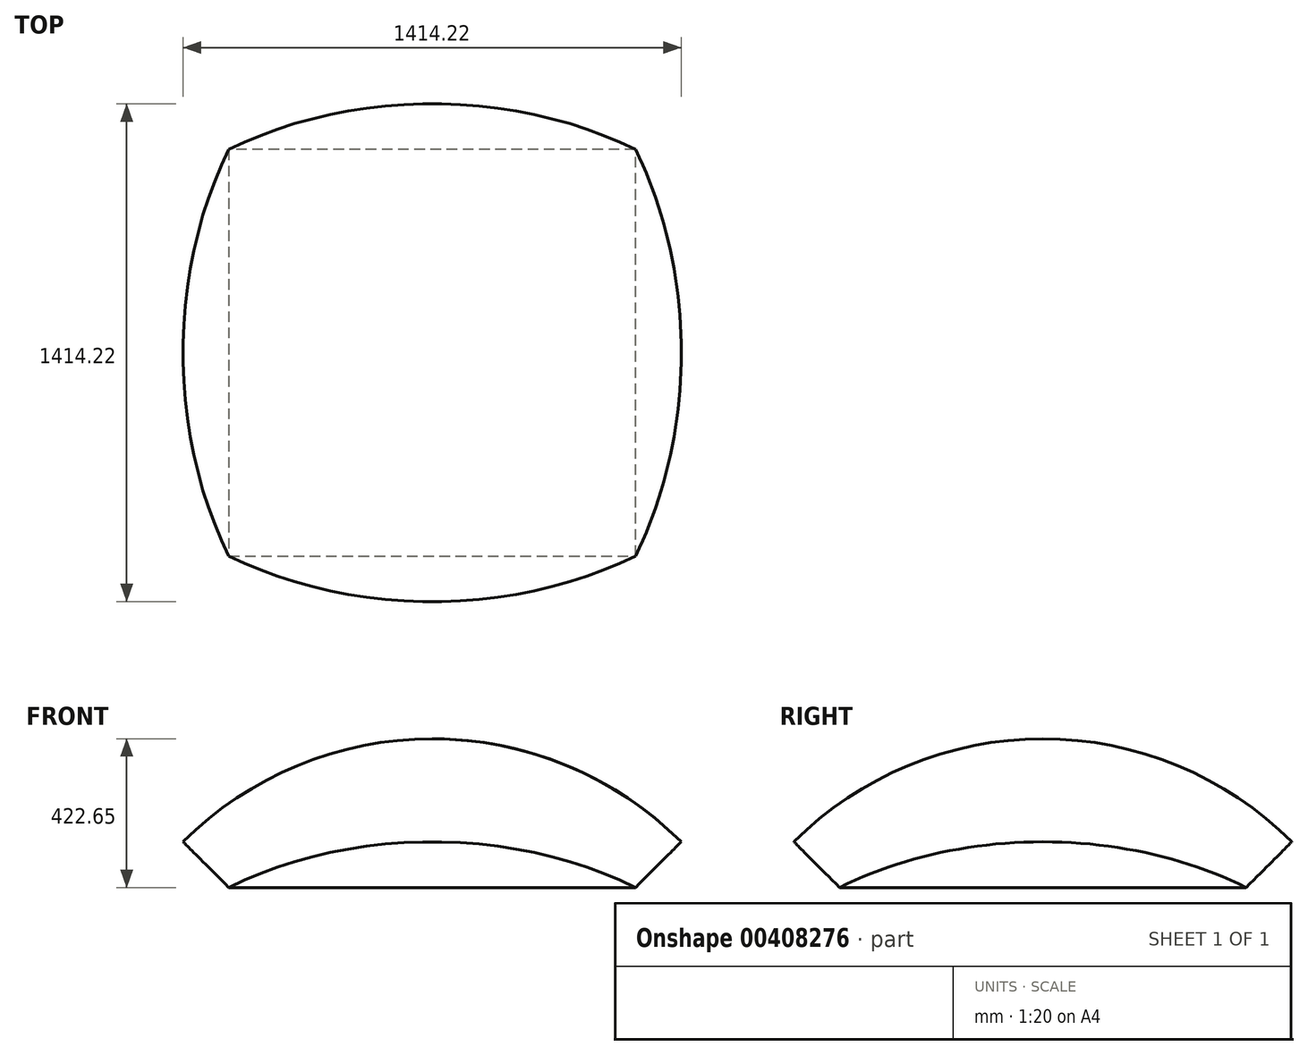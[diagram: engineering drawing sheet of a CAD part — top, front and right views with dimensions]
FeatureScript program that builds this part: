
annotation { "Feature Type Name" : "Feature", "Feature Type Description" : "" }
export const myFeature = defineFeature(function(context is Context, id is Id, definition is map)
    precondition{}
    {
        {
            var Q0;
            Q0=qCreatedBy(makeId("Front.planeOp"),FACE);
            var sketch = newSketch(context, id + "F0", { "sketchPlane" : qUnion([Q0])});
            skArc(sketch, "E0", {"start": v(0, 1000) * mm, "mid": v(-1000, 0) * mm, "end": v(0, -1000) * mm});
            skLineSegment(sketch, "E1", {"start": v(0, 1000) * mm, "end": v(0, -1000) * mm});
            skSolve(sketch);
        }
        {
            var Q0;
            Q0 = qSketchRegion(id + "F0", true);
            var Q1;
            Q1=sQuery(id+"F0.wireOp",EDGE,"E1");
            revolve(context, id + "F1", {"entities" : qUnion([Q0]), "axis" : qUnion([Q1]), "revolveType" : RevolveType.FULL});
        }
        {
            var Q0;
            Q0=qCreatedBy(makeId("Front.planeOp"),FACE);
            var sketch = newSketch(context, id + "F2", { "sketchPlane" : qUnion([Q0])});
            skLineSegment(sketch, "E2", {"start": v(-1100, 1100) * mm, "end": v(-1100, -1100) * mm});
            skLineSegment(sketch, "E3", {"start": v(1100, -1100) * mm, "end": v(1100, 1100) * mm});
            skLineSegment(sketch, "E4", {"start": v(1100, 1100) * mm, "end": v(0, 0) * mm});
            skLineSegment(sketch, "E5", {"start": v(0, 0) * mm, "end": v(-1100, 1100) * mm});
            skLineSegment(sketch, "E6", {"start": v(-1100, -1100) * mm, "end": v(1100, -1100) * mm});
            skSolve(sketch);
        }
        {
            var Q0;
            Q0 = qSketchRegion(id + "F2", true);
            extrude(context, id + "F3", {"entities" : qUnion([Q0]), "operationType" : NewBodyOperationType.REMOVE, "endBound" : BoundingType.SYMMETRIC, "oppositeDirection" : true, "depth" : 2200 * mm, "hasSecondDirection" : true, "secondDirectionBound" : SecondDirectionBoundingType.THROUGH_ALL, "secondDirectionOppositeDirection" : false, "secondDirectionDepth" : 25 * mm});
        }
        {
            var Q0;
            Q0=qCreatedBy(makeId("Right.planeOp"),FACE);
            var sketch = newSketch(context, id + "F4", { "sketchPlane" : qUnion([Q0])});
            skLineSegment(sketch, "E7", {"start": v(-1100, 1100) * mm, "end": v(-1100, -1100) * mm});
            skLineSegment(sketch, "E8", {"start": v(1100, -1100) * mm, "end": v(1100, 1100) * mm});
            skLineSegment(sketch, "E9", {"start": v(1100, 1100) * mm, "end": v(0, 0) * mm});
            skLineSegment(sketch, "E10", {"start": v(0, 0) * mm, "end": v(-1100, 1100) * mm});
            skLineSegment(sketch, "E11", {"start": v(-1100, -1100) * mm, "end": v(1100, -1100) * mm});
            skSolve(sketch);
        }
        {
            var Q0;
            Q0 = qSketchRegion(id + "F4", true);
            extrude(context, id + "F5", {"entities" : qUnion([Q0]), "operationType" : NewBodyOperationType.REMOVE, "endBound" : BoundingType.SYMMETRIC, "oppositeDirection" : true, "depth" : 2200 * mm});
        }
        {
            var Q0;
            Q0=qCreatedBy(makeId("Top.planeOp"),FACE);
            var sketch = newSketch(context, id + "F6", { "sketchPlane" : qUnion([Q0])});
            skCircle(sketch, "E12", {"center": v(0, 0) * mm, "radius": 1000 * mm});
            skSolve(sketch);
        }
        {
            var Q0;
            Q0 = qSketchRegion(id + "F6", true);
            var Q1;
            Q1=makeQuery(id+"F5.boolean.opBoolean","INTERSECT",VERTEX,{"derivedFrom":[makeQuery(id+"F3.boolean.opBoolean","COPY",FACE,{"derivedFrom":makeQuery(id+"F3.opExtrude","SWEPT_FACE",FACE,{"disambiguationData":[OSD([sQuery(id+"F2.wireOp",EDGE,"E4")])]})}),makeQuery(id+"F1.opRevolve","SWEPT_FACE",FACE,{"disambiguationData":[OSD([sQuery(id+"F0.wireOp",EDGE,"E0")])]}),makeQuery(id+"F5.opExtrude","SWEPT_FACE",FACE,{"disambiguationData":[OSD([sQuery(id+"F4.wireOp",EDGE,"E10")])]})]});
            extrude(context, id + "F7", {"entities" : qUnion([Q0]), "operationType" : NewBodyOperationType.REMOVE, "endBound" : BoundingType.UP_TO_VERTEX, "endBoundEntityVertex" : qUnion([Q1]), "depth" : 25 * mm});
        }
    });
